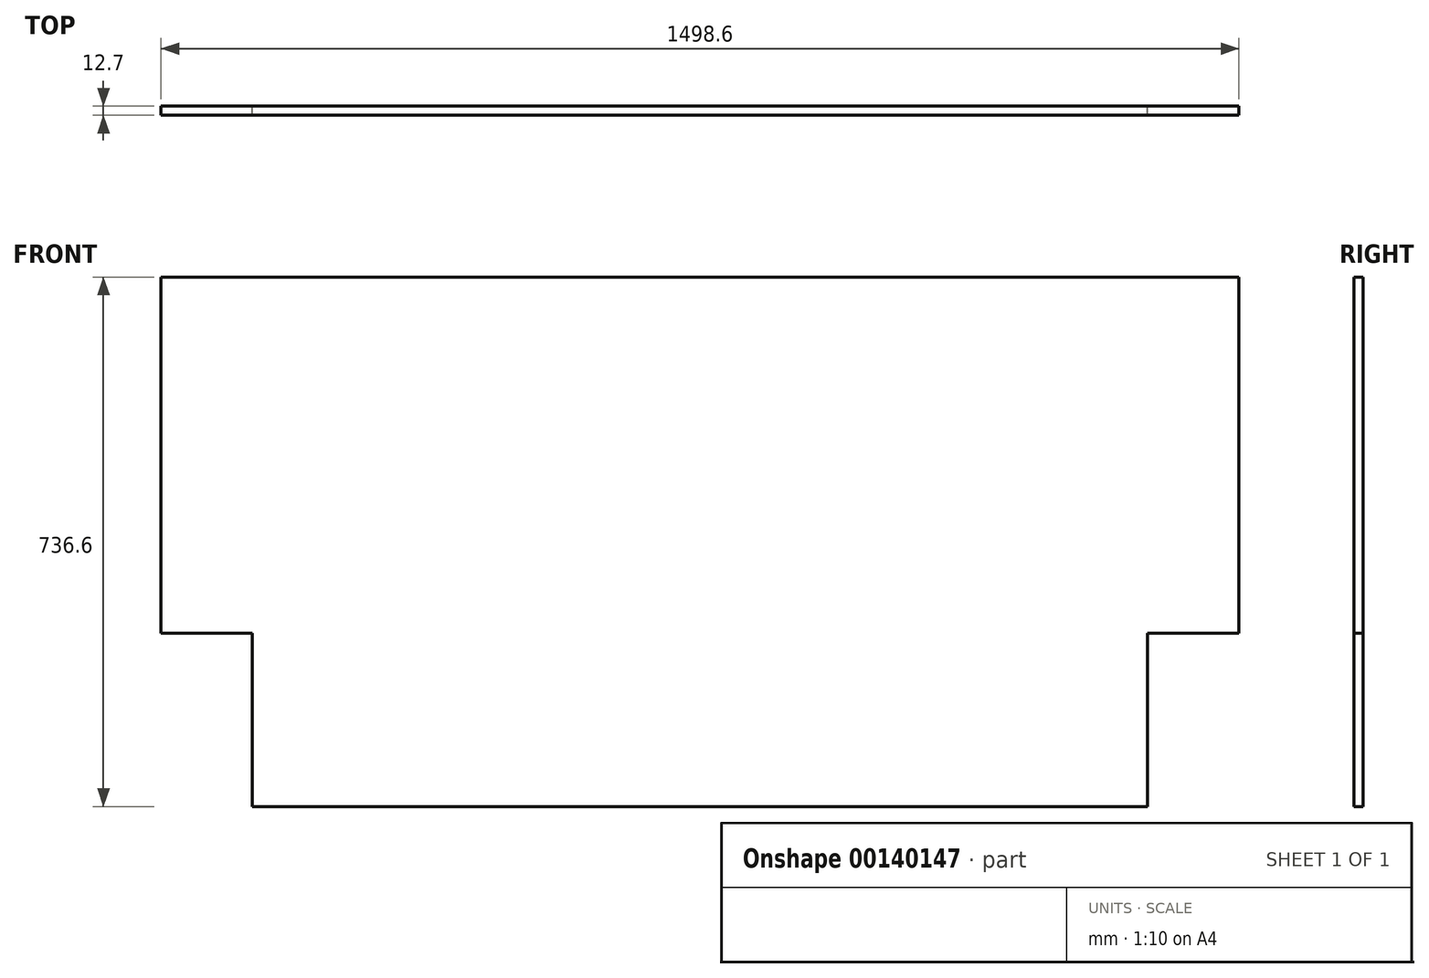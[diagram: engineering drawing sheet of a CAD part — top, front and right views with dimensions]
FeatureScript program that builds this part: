
annotation { "Feature Type Name" : "Feature", "Feature Type Description" : "" }
export const myFeature = defineFeature(function(context is Context, id is Id, definition is map)
    precondition{}
    {
        {
            var Q0;
            Q0=qCreatedBy(makeId("Front.planeOp"),FACE);
            var sketch = newSketch(context, id + "F0", { "sketchPlane" : qUnion([Q0])});
            skLineSegment(sketch, "E0", {"start": v(-622.3, 254) * mm, "end": v(-622.3, 12.7) * mm});
            skLineSegment(sketch, "E1", {"start": v(-749.3, 254) * mm, "end": v(-749.3, 749.3) * mm});
            skLineSegment(sketch, "E2", {"start": v(749.3, 254) * mm, "end": v(749.3, 749.3) * mm});
            skLineSegment(sketch, "E3", {"start": v(622.3, 12.7) * mm, "end": v(-622.3, 12.7) * mm});
            skLineSegment(sketch, "E4", {"start": v(-749.3, 749.3) * mm, "end": v(749.3, 749.3) * mm});
            skLineSegment(sketch, "E5", {"start": v(622.3, 12.7) * mm, "end": v(622.3, 254) * mm});
            skLineSegment(sketch, "E6", {"start": v(-749.3, 254) * mm, "end": v(-622.3, 254) * mm});
            skLineSegment(sketch, "E7.trimOffspring", {"start": v(622.3, 254) * mm, "end": v(749.3, 254) * mm});
            skSolve(sketch);
        }
        {
            var Q0;
            Q0=makeQuery(id+"F0.imprint","IMPRINT",FACE,{"disambiguationData":[TD([[makeQuery(id+"F0.imprint","IMPRINT",EDGE,{"derivedFrom":sQuery(id+"F0.wireOp",EDGE,"E0")}),1.0]])]});
            extrude(context, id + "F1", {"entities" : qUnion([Q0]), "depth" : 12.7 * mm});
        }
    });
